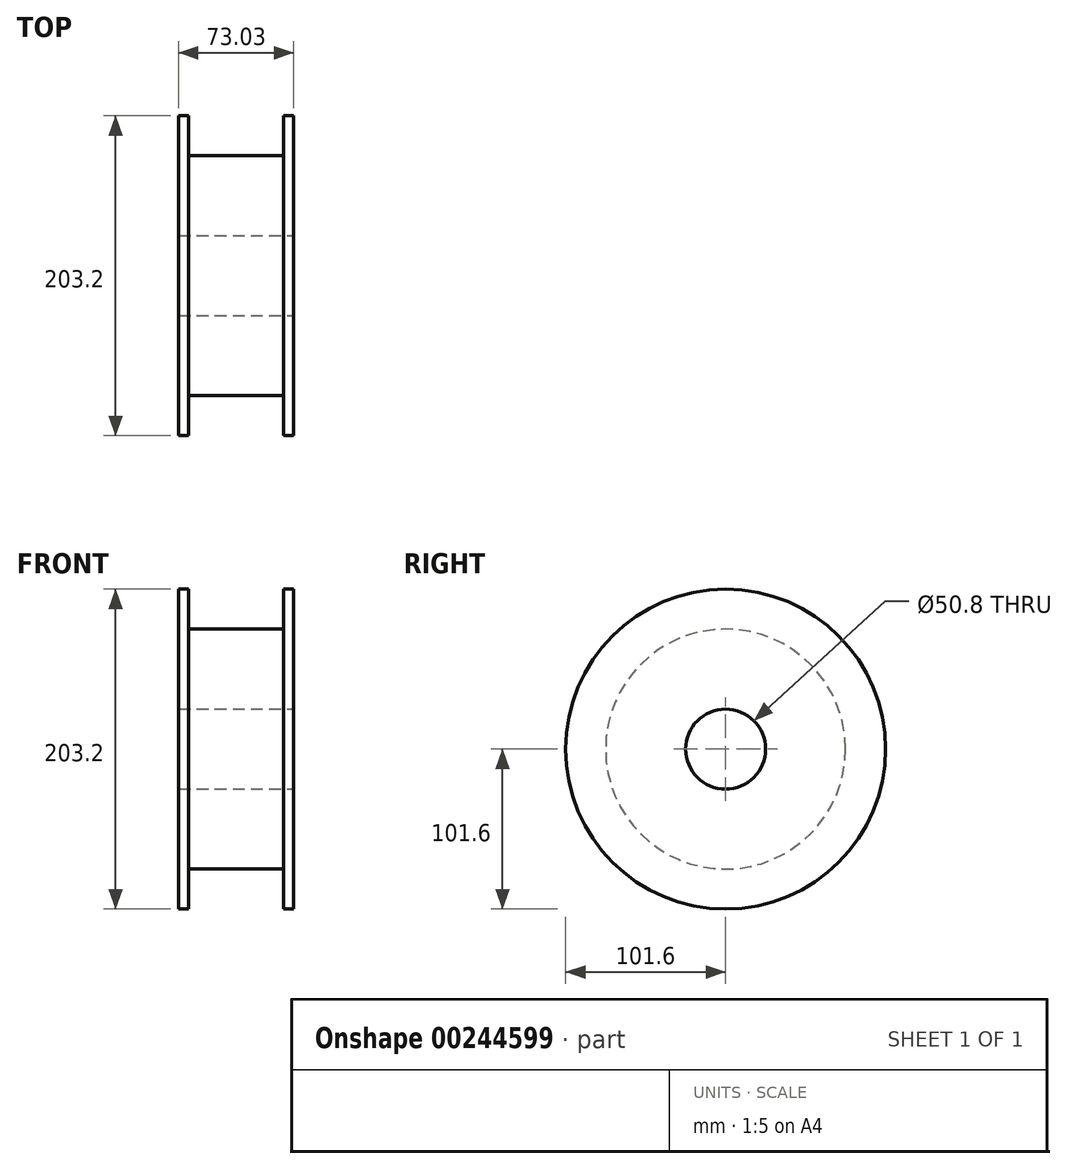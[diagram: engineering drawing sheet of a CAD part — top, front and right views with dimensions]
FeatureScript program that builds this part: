
annotation { "Feature Type Name" : "Feature", "Feature Type Description" : "" }
export const myFeature = defineFeature(function(context is Context, id is Id, definition is map)
    precondition{}
    {
        {
            var Q0;
            Q0=qCreatedBy(makeId("Right.planeOp"),FACE);
            var sketch = newSketch(context, id + "F0", { "sketchPlane" : qUnion([Q0])});
            skCircle(sketch, "E0", {"center": v(0, 0) * mm, "radius": 101.6 * mm});
            skSolve(sketch);
        }
        {
            var Q0;
            Q0 = qSketchRegion(id + "F0", true);
            extrude(context, id + "F1", {"entities" : qUnion([Q0]), "depth" : 6.35 * mm});
        }
        {
            var Q0;
            Q0=makeQuery(id+"F1.opExtrude","CAP_FACE",FACE,{"disambiguationData":[OSD([sQuery(id+"F0.wireOp",EDGE,"E0")])],"isStart":false});
            var sketch = newSketch(context, id + "F2", { "sketchPlane" : qUnion([Q0])});
            skCircle(sketch, "E1", {"center": v(0, 0) * mm, "radius": 76.2 * mm});
            skSolve(sketch);
        }
        {
            var Q0;
            Q0 = qSketchRegion(id + "F2", true);
            extrude(context, id + "F3", {"entities" : qUnion([Q0]), "operationType" : NewBodyOperationType.ADD, "depth" : 60.32 * mm});
        }
        {
            var Q0;
            Q0=makeQuery(id+"F3.opExtrude","CAP_FACE",FACE,{"disambiguationData":[OSD([sQuery(id+"F2.wireOp",EDGE,"E1")])],"isStart":false});
            var sketch = newSketch(context, id + "F4", { "sketchPlane" : qUnion([Q0])});
            skCircle(sketch, "E2", {"center": v(0, 0) * mm, "radius": 101.6 * mm});
            skSolve(sketch);
        }
        {
            var Q0;
            Q0 = qSketchRegion(id + "F4", true);
            extrude(context, id + "F5", {"entities" : qUnion([Q0]), "operationType" : NewBodyOperationType.ADD, "depth" : 6.35 * mm});
        }
        {
            var Q0;
            Q0=makeQuery(id+"F5.opExtrude","CAP_FACE",FACE,{"disambiguationData":[OSD([sQuery(id+"F4.wireOp",EDGE,"E2")])],"isStart":false});
            var sketch = newSketch(context, id + "F6", { "sketchPlane" : qUnion([Q0])});
            skCircle(sketch, "E3", {"center": v(0, 0) * mm, "radius": 25.4 * mm});
            skSolve(sketch);
        }
        {
            var Q0;
            Q0 = qSketchRegion(id + "F6", true);
            extrude(context, id + "F7", {"entities" : qUnion([Q0]), "operationType" : NewBodyOperationType.REMOVE, "endBound" : BoundingType.THROUGH_ALL, "oppositeDirection" : true, "depth" : 25.4 * mm});
        }
    });
